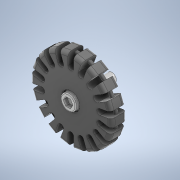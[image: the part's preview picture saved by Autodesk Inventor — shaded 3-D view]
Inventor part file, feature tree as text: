
AUTODESK INVENTOR PART (.ipt)
format: ipt  version: 2021 (Build 250183000, 183)  size: 544,768 bytes
history: native  units: mm
features: extrude x7, sketch x7, projected_geometry x2, pattern_circular x1, fillet x1
ambient origin geometry x8: Origin, YZ Plane, XZ Plane, XY Plane, X Axis, Y Axis, Z Axis, Center Point
bodies: Solid1 (feature_tree)
feature tree (18):
  extrude  "Extrusion1"  Depth=10.0mm
  extrude  "Extrusion2"  Depth=3.35mm
  extrude  "Extrusion3"  TaperAngle=0.0deg  [1 undecoded]
  pattern_circular  "Circular Pattern1"  Count=18 Angle=360.0deg
  extrude  "Extrusion4"  Depth=8.5mm
  extrude  "Extrusion5"  Depth=2.0mm
  extrude  "Extrusion6"  Depth=2.1mm
  extrude  "Extrusion7"  Depth=0.5mm TaperAngle=360.0deg
  fillet  "Fillet1"  Radius=8.5mm
  sketch  "Sketch1"  dims[d0=45.0mm d1=10.0mm]
  sketch  "Sketch2"  dims[d2=3.2mm d3=3.35mm]
  sketch  "Sketch3"  dims[d4=19.6mm d5=0.0mm d6=180.0mm d8=360.0deg]
  projected_geometry  "Projected Loop1"
  sketch  "Sketch4"  dims[d10=8.5mm d11=0.0mm d12=27.0mm]
  sketch  "Sketch5"  dims[d13=2.0mm d14=0.0mm d15=4.6mm]
  projected_geometry  "Projected Loop2"
  sketch  "Sketch6"  dims[d16=1.9mm d17=2.1mm]
  sketch  "Sketch7"  dims[d18=3.2mm d19=0.0mm d20=180.0mm d21=360.0deg d23=8.5mm d24=1.5mm d25=1.7mm d26=0.0mm d27=0.0mm d28=4.6mm d29=2.0mm d30=0.0mm d31=21.0mm d32=0.0mm d33=5.0mm d34=30.0mm d35=0.0mm d36=2.0mm d37=0.5mm]
note: 1 required parameter value undecoded (feature->parameter linkage not recoverable at this tier; creation-order binding heuristic only, values carry confidence <= 0.55)
